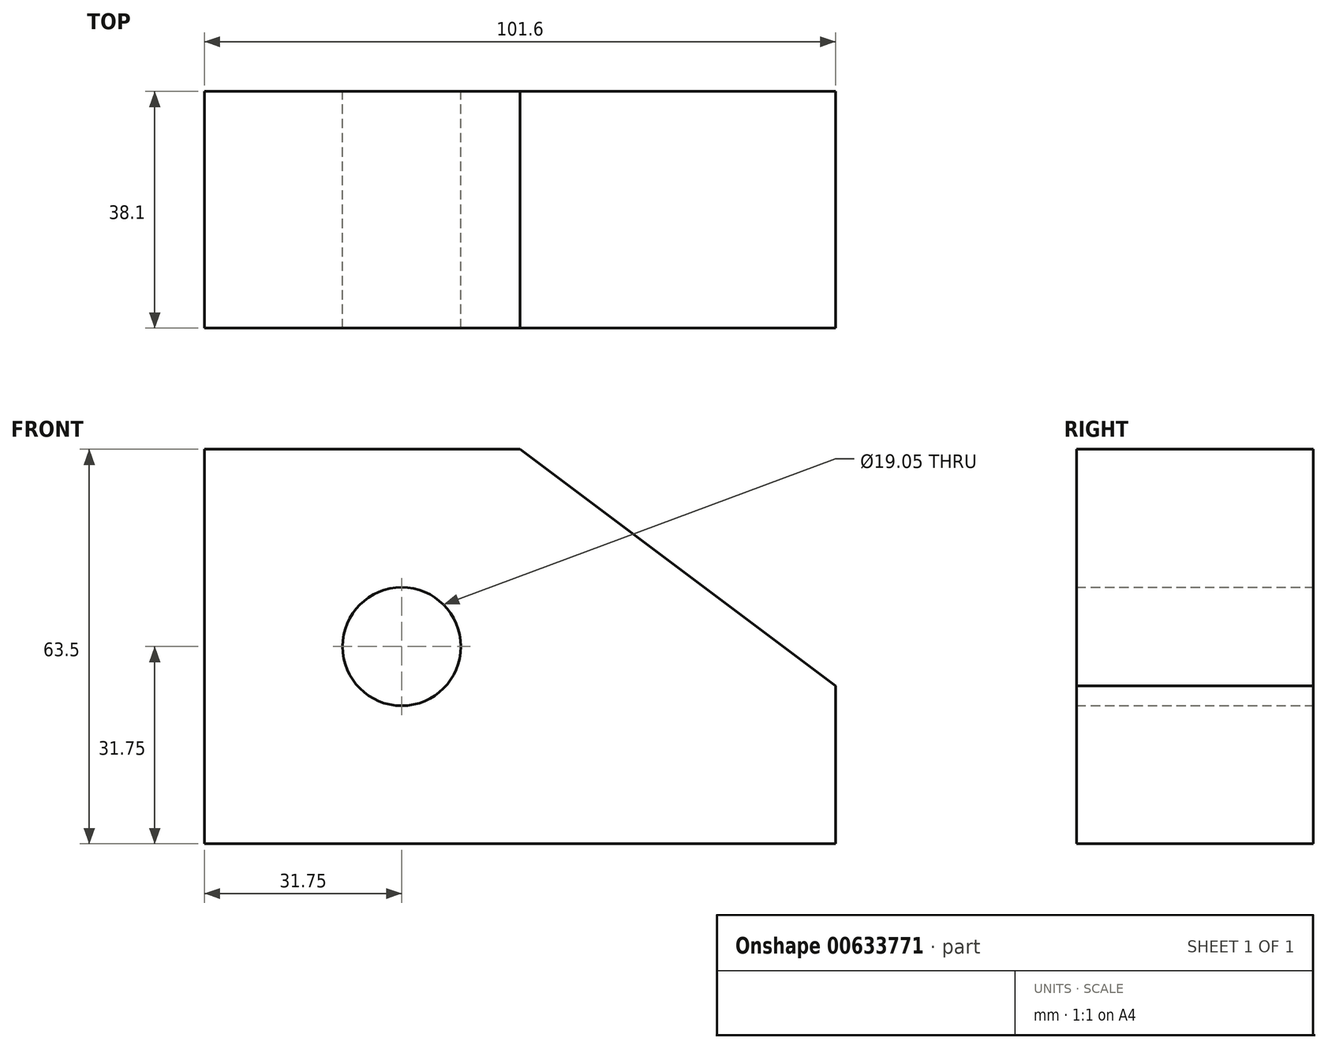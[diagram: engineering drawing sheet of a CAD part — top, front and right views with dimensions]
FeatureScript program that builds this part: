
annotation { "Feature Type Name" : "Feature", "Feature Type Description" : "" }
export const myFeature = defineFeature(function(context is Context, id is Id, definition is map)
    precondition{}
    {
        {
            var Q0;
            Q0=qCreatedBy(makeId("Front.planeOp"),FACE);
            var sketch = newSketch(context, id + "F0", { "sketchPlane" : qUnion([Q0])});
            skLineSegment(sketch, "E0", {"start": v(0, 0) * mm, "end": v(0, 63.5) * mm});
            skLineSegment(sketch, "E1", {"start": v(0, 63.5) * mm, "end": v(50.8, 63.5) * mm});
            skLineSegment(sketch, "E2", {"start": v(0, 0) * mm, "end": v(101.6, 0) * mm});
            skLineSegment(sketch, "E3", {"start": v(101.6, 0) * mm, "end": v(101.6, 25.4) * mm});
            skLineSegment(sketch, "E4", {"start": v(101.6, 25.4) * mm, "end": v(50.8, 63.5) * mm});
            skPoint(sketch, "E5.centerSnap0", {"position": v(0, 31.75) * mm});
            skCircle(sketch, "E6", {"center": v(31.75, 31.75) * mm, "radius": 9.53 * mm});
            skSolve(sketch);
        }
        {
            var Q0;
            Q0 = qSketchRegion(id + "F0", true);
            extrude(context, id + "F1", {"entities" : qUnion([Q0]), "depth" : 38.1 * mm, "offsetDistance" : 25.4 * mm});
        }
    });
